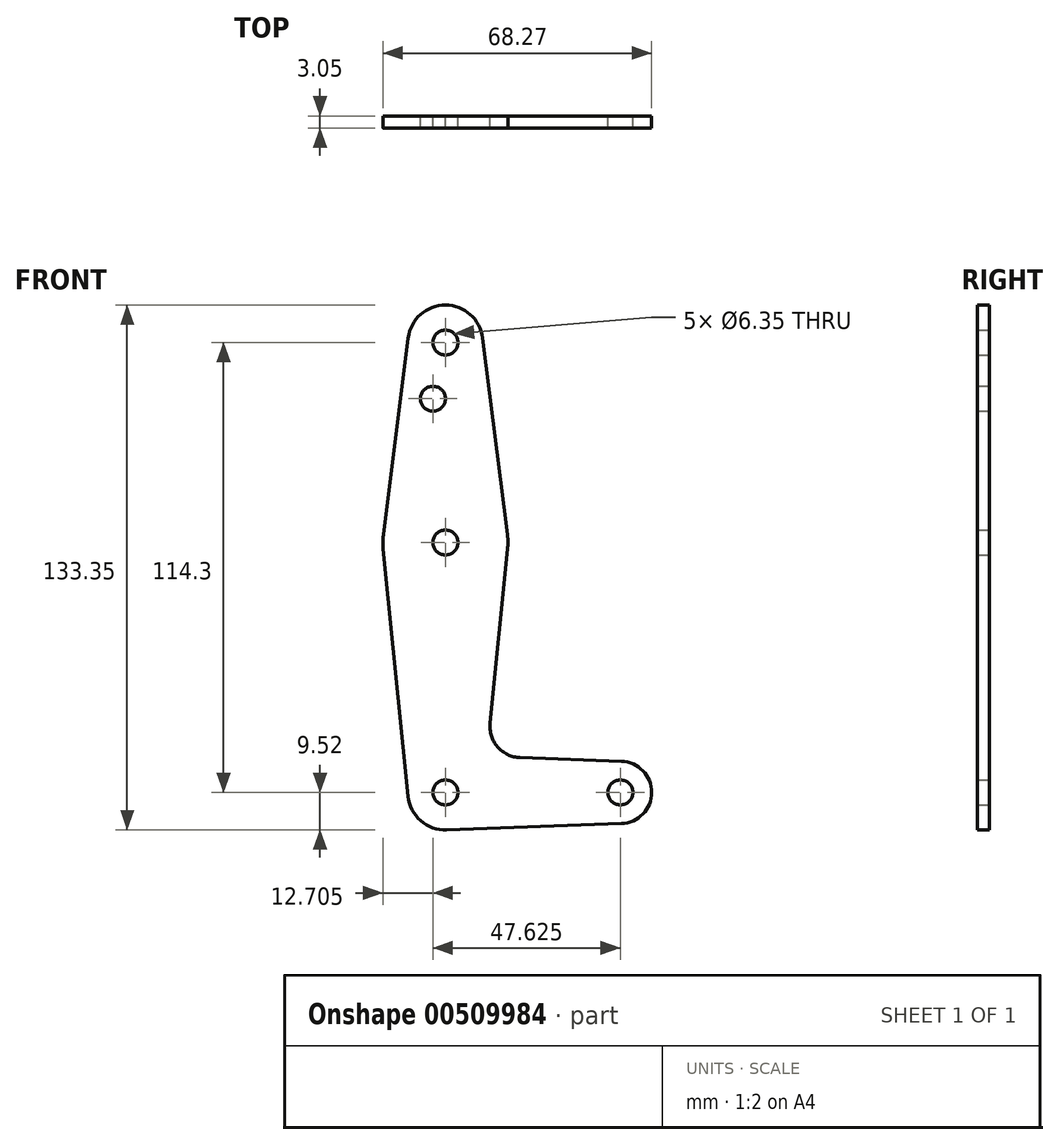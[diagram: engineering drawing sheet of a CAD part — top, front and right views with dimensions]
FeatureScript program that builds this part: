
annotation { "Feature Type Name" : "Feature", "Feature Type Description" : "" }
export const myFeature = defineFeature(function(context is Context, id is Id, definition is map)
    precondition{}
    {
        {
            var Q0;
            Q0=qCreatedBy(makeId("Front.planeOp"),FACE);
            var sketch = newSketch(context, id + "F0", { "sketchPlane" : qUnion([Q0])});
            skLineSegment(sketch, "E0", {"start": v(0, 0) * mm, "end": v(0, 114.3) * mm, "construction": true});
            skLineSegment(sketch, "E1", {"start": v(0, 0) * mm, "end": v(44.45, 0) * mm, "construction": true});
            skCircle(sketch, "E2", {"center": v(0, 114.3) * mm, "radius": 9.53 * mm});
            skCircle(sketch, "E3", {"center": v(0, 0) * mm, "radius": 9.53 * mm});
            skCircle(sketch, "E4", {"center": v(0, 63.5) * mm, "radius": 15.88 * mm});
            skCircle(sketch, "E5", {"center": v(44.45, 0) * mm, "radius": 7.94 * mm});
            skLineSegment(sketch, "E6", {"start": v(-15.75, 65.48) * mm, "end": v(-9.45, 115.5) * mm});
            skLineSegment(sketch, "E7", {"start": v(9.45, 115.5) * mm, "end": v(15.75, 65.48) * mm});
            skLineSegment(sketch, "E8", {"start": v(-15.8, 61.91) * mm, "end": v(-9.48, -0.95) * mm});
            skLineSegment(sketch, "E9", {"start": v(11.34, 17.6) * mm, "end": v(15.8, 61.91) * mm});
            skLineSegment(sketch, "E10", {"start": v(18.97, 8.85) * mm, "end": v(44.73, 7.93) * mm});
            skLineSegment(sketch, "E11", {"start": v(0.34, -9.52) * mm, "end": v(44.73, -7.93) * mm});
            skArc(sketch, "E12.filletArc", {"start": v(11.34, 17.6) * mm, "mid": v(13.26, 11.57) * mm, "end": v(18.97, 8.85) * mm});
            skCircle(sketch, "E13", {"center": v(0, 114.3) * mm, "radius": 3.18 * mm});
            skCircle(sketch, "E14", {"center": v(0, 63.5) * mm, "radius": 3.18 * mm});
            skCircle(sketch, "E15", {"center": v(0, 0) * mm, "radius": 3.18 * mm});
            skCircle(sketch, "E16", {"center": v(44.45, 0) * mm, "radius": 3.18 * mm});
            skCircle(sketch, "E17", {"center": v(-3.18, 100.03) * mm, "radius": 3.18 * mm});
            skSolve(sketch);
        }
        {
            var Q0;
            {var subQ0=sQuery(id+"F0.wireOp",EDGE,"E8");Q0=makeQuery(id+"F0.imprint","IMPRINT",FACE,{"disambiguationData":[TD([[makeQuery(id+"F0.imprint","IMPRINT",EDGE,{"derivedFrom":subQ0}),1.0]])]});}
            var Q1;
            Q1=makeQuery(id+"F0.imprint","IMPRINT",FACE,{"disambiguationData":[TD([[makeQuery(id+"F0.imprint","IMPRINT",EDGE,{"derivedFrom":sQuery(id+"F0.wireOp",EDGE,"E14")}),-1.0]])]});
            var Q2;
            {var subQ0=sQuery(id+"F0.wireOp",EDGE,"E6");Q2=makeQuery(id+"F0.imprint","IMPRINT",FACE,{"disambiguationData":[TD([[makeQuery(id+"F0.imprint","IMPRINT",EDGE,{"derivedFrom":subQ0}),-1.0]])]});}
            var Q3;
            Q3=makeQuery(id+"F0.imprint","IMPRINT",FACE,{"disambiguationData":[TD([[makeQuery(id+"F0.imprint","IMPRINT",EDGE,{"derivedFrom":sQuery(id+"F0.wireOp",EDGE,"E13")}),-1.0]])]});
            var Q4;
            Q4=makeQuery(id+"F0.imprint","IMPRINT",FACE,{"disambiguationData":[TD([[makeQuery(id+"F0.imprint","IMPRINT",EDGE,{"derivedFrom":sQuery(id+"F0.wireOp",EDGE,"E16")}),-1.0]])]});
            var Q5;
            Q5=makeQuery(id+"F0.imprint","IMPRINT",FACE,{"disambiguationData":[TD([[makeQuery(id+"F0.imprint","IMPRINT",EDGE,{"derivedFrom":sQuery(id+"F0.wireOp",EDGE,"E15")}),-1.0]])]});
            extrude(context, id + "F1", {"entities" : qUnion([Q0, Q1, Q2, Q3, Q4, Q5]), "depth" : 3.05 * mm});
        }
    });
